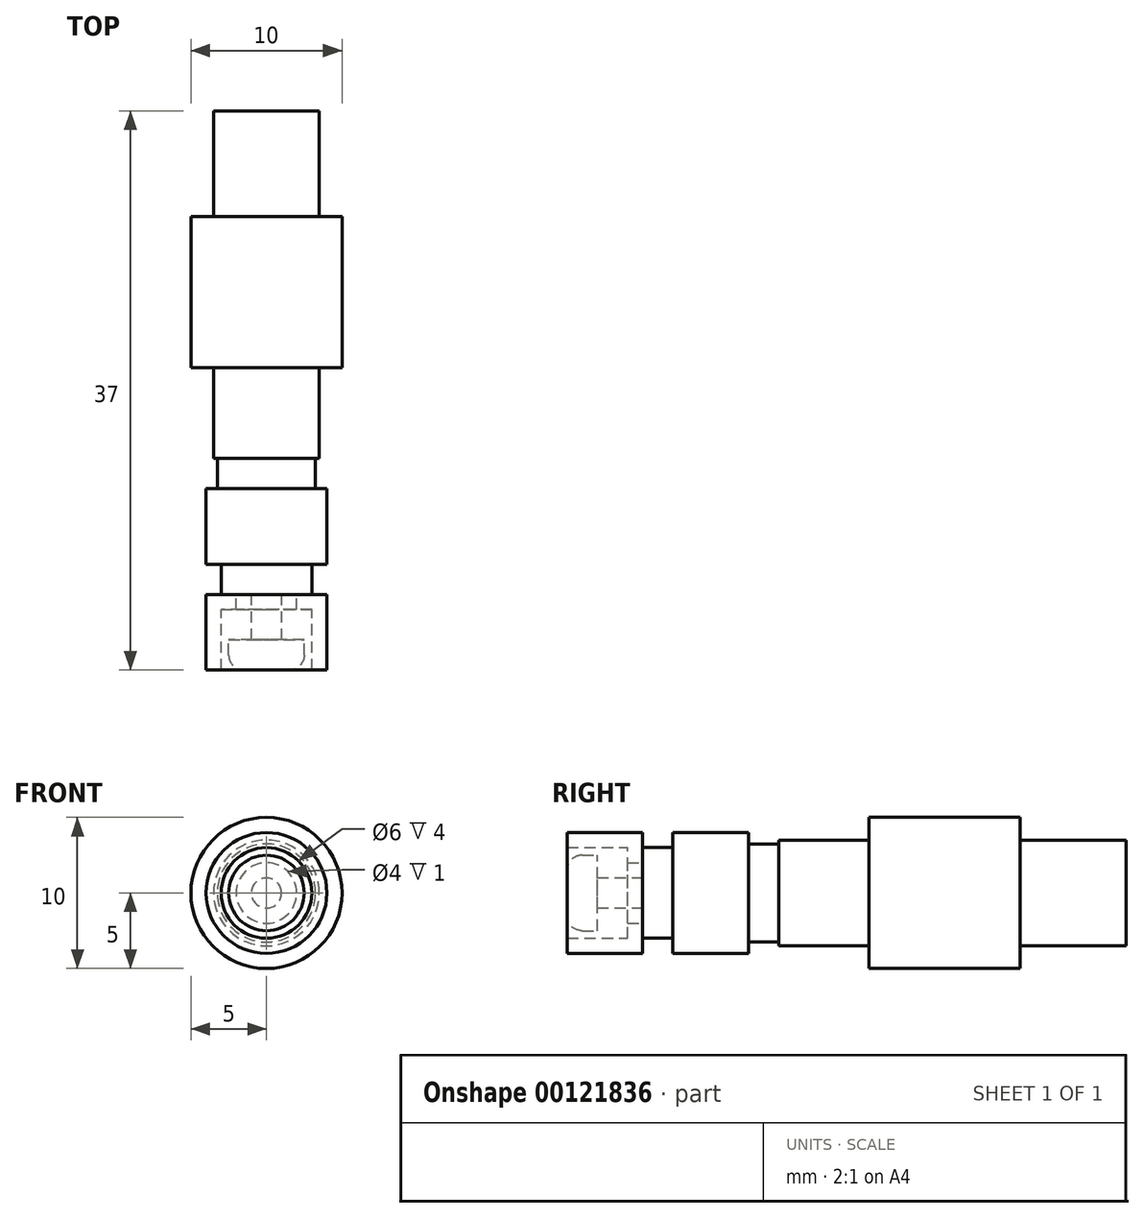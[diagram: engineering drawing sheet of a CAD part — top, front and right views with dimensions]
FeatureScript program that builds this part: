
annotation { "Feature Type Name" : "Feature", "Feature Type Description" : "" }
export const myFeature = defineFeature(function(context is Context, id is Id, definition is map)
    precondition{}
    {
        {
            var Q0;
            Q0=qCreatedBy(makeId("Front.planeOp"),FACE);
            var sketch = newSketch(context, id + "F0", { "sketchPlane" : qUnion([Q0])});
            skCircle(sketch, "E0", {"center": v(0, 0) * mm, "radius": 4 * mm});
            skSolve(sketch);
        }
        {
            var Q0;
            Q0=makeQuery(id+"F0.imprint","IMPRINT",FACE,{"disambiguationData":[TD([[makeQuery(id+"F0.imprint","IMPRINT",EDGE,{"derivedFrom":sQuery(id+"F0.wireOp",EDGE,"E0")}),1.0]])]});
            extrude(context, id + "F1", {"entities" : qUnion([Q0]), "depth" : 5 * mm});
        }
        {
            var Q0;
            Q0=makeQuery(id+"F1.opExtrude","CAP_FACE",FACE,{"disambiguationData":[OSD([sQuery(id+"F0.wireOp",EDGE,"E0")])],"isStart":false});
            var sketch = newSketch(context, id + "F2", { "sketchPlane" : qUnion([Q0])});
            skCircle(sketch, "E1", {"center": v(0, 0) * mm, "radius": 3 * mm});
            skSolve(sketch);
        }
        {
            var Q0;
            Q0=makeQuery(id+"F2.imprint","IMPRINT",FACE,{"disambiguationData":[TD([[makeQuery(id+"F2.imprint","IMPRINT",EDGE,{"derivedFrom":sQuery(id+"F2.wireOp",EDGE,"E1")}),1.0]])]});
            extrude(context, id + "F3", {"entities" : qUnion([Q0]), "operationType" : NewBodyOperationType.ADD, "depth" : 2 * mm});
        }
        {
            var Q0;
            Q0=makeQuery(id+"F3.opExtrude","CAP_FACE",FACE,{"disambiguationData":[OSD([sQuery(id+"F2.wireOp",EDGE,"E1")])],"isStart":false});
            var sketch = newSketch(context, id + "F4", { "sketchPlane" : qUnion([Q0])});
            skCircle(sketch, "E2", {"center": v(0, 0) * mm, "radius": 4 * mm});
            skCircle(sketch, "E3", {"center": v(0, 0) * mm, "radius": 2 * mm});
            skSolve(sketch);
        }
        {
            var Q0;
            Q0=makeQuery(id+"F4.imprint","IMPRINT",FACE,{"disambiguationData":[TD([[makeQuery(id+"F4.imprint","IMPRINT",EDGE,{"derivedFrom":sQuery(id+"F4.wireOp",EDGE,"E2")}),1.0]])]});
            var Q1;
            Q1=sQuery(id+"F4.wireOp",EDGE,"E2");
            extrude(context, id + "F5", {"entities" : qUnion([Q0]), "surfaceEntities" : qUnion([Q1]), "depth" : 5 * mm});
        }
        {
            var Q0;
            Q0=makeQuery(id+"F3.opExtrude","CAP_FACE",FACE,{"disambiguationData":[OSD([sQuery(id+"F2.wireOp",EDGE,"E1")])],"isStart":false});
            var sketch = newSketch(context, id + "F6", { "sketchPlane" : qUnion([Q0])});
            skCircle(sketch, "E4", {"center": v(0, 0) * mm, "radius": 1 * mm});
            skSolve(sketch);
        }
        {
            var Q0;
            Q0=makeQuery(id+"F6.imprint","IMPRINT",FACE,{"disambiguationData":[TD([[makeQuery(id+"F6.imprint","IMPRINT",EDGE,{"derivedFrom":sQuery(id+"F6.wireOp",EDGE,"E4")}),1.0]])]});
            var Q1;
            Q1=sQuery(id+"F6.wireOp",EDGE,"E4");
            extrude(context, id + "F7", {"entities" : qUnion([Q0]), "operationType" : NewBodyOperationType.ADD, "surfaceEntities" : qUnion([Q1]), "depth" : 3 * mm});
        }
        {
            var Q0;
            Q0=makeQuery(id+"F7.opExtrude","CAP_FACE",FACE,{"disambiguationData":[OSD([sQuery(id+"F6.wireOp",EDGE,"E4")])],"isStart":false});
            var sketch = newSketch(context, id + "F8", { "sketchPlane" : qUnion([Q0])});
            skCircle(sketch, "E5", {"center": v(0, 0) * mm, "radius": 2.5 * mm});
            skSolve(sketch);
        }
        {
            var Q0;
            Q0=makeQuery(id+"F8.imprint","IMPRINT",FACE,{"disambiguationData":[TD([[makeQuery(id+"F8.imprint","IMPRINT",EDGE,{"derivedFrom":sQuery(id+"F8.wireOp",EDGE,"E5")}),1.0]])]});
            var Q1;
            Q1=makeQuery(id+"F8.imprint","IMPRINT",FACE,{"disambiguationData":[TD([[makeQuery(id+"F8.imprint","IMPRINT",EDGE,{"derivedFrom":makeQuery(id+"F7.opExtrude","CAP_EDGE",EDGE,{"disambiguationData":[OSD([sQuery(id+"F6.wireOp",EDGE,"E4")])],"isStart":false})}),1.0]])]});
            extrude(context, id + "F9", {"entities" : qUnion([Q0, Q1]), "operationType" : NewBodyOperationType.ADD, "depth" : 2 * mm});
        }
        {
            var Q0;
            Q0=makeQuery(id+"F9.opExtrude","CAP_EDGE",EDGE,{"disambiguationData":[OSD([sQuery(id+"F8.wireOp",EDGE,"E5")])],"isStart":false});
            fillet(context, id + "F10", {"entities" : qUnion([Q0]), "radius" : 1 * mm, "tangentPropagation" : true, "allowEdgeOverflow" : false});
        }
        {
            var Q0;
            Q0=makeQuery(id+"F4.imprint","IMPRINT",FACE,{"disambiguationData":[TD([[makeQuery(id+"F4.imprint","IMPRINT",EDGE,{"derivedFrom":sQuery(id+"F4.wireOp",EDGE,"E2")}),1.0]])]});
            var Q1;
            Q1=makeQuery(id+"F4.imprint","IMPRINT",FACE,{"disambiguationData":[TD([[makeQuery(id+"F4.imprint","IMPRINT",EDGE,{"derivedFrom":sQuery(id+"F4.wireOp",EDGE,"E3")}),-1.0]])]});
            extrude(context, id + "F11", {"entities" : qUnion([Q0, Q1]), "operationType" : NewBodyOperationType.ADD, "depth" : 1 * mm});
        }
        {
            var Q0;
            Q0=makeQuery(id+"F1.opExtrude","CAP_FACE",FACE,{"disambiguationData":[OSD([sQuery(id+"F0.wireOp",EDGE,"E0")])],"isStart":true});
            var sketch = newSketch(context, id + "F12", { "sketchPlane" : qUnion([Q0])});
            skCircle(sketch, "E6", {"center": v(0, 0) * mm, "radius": 3.25 * mm});
            skSolve(sketch);
        }
        {
            var Q0;
            Q0=makeQuery(id+"F12.imprint","IMPRINT",FACE,{"disambiguationData":[TD([[makeQuery(id+"F12.imprint","IMPRINT",EDGE,{"derivedFrom":sQuery(id+"F12.wireOp",EDGE,"E6")}),1.0]])]});
            extrude(context, id + "F13", {"entities" : qUnion([Q0]), "operationType" : NewBodyOperationType.ADD, "depth" : 2 * mm});
        }
        {
            var Q0;
            Q0=makeQuery(id+"F13.opExtrude","CAP_FACE",FACE,{"disambiguationData":[OSD([sQuery(id+"F12.wireOp",EDGE,"E6")])],"isStart":false});
            var sketch = newSketch(context, id + "F14", { "sketchPlane" : qUnion([Q0])});
            skCircle(sketch, "E7", {"center": v(0, 0) * mm, "radius": 3.5 * mm});
            skSolve(sketch);
        }
        {
            var Q0;
            Q0=makeQuery(id+"F14.imprint","IMPRINT",FACE,{"disambiguationData":[TD([[makeQuery(id+"F14.imprint","IMPRINT",EDGE,{"derivedFrom":sQuery(id+"F14.wireOp",EDGE,"E7")}),1.0]])]});
            var Q1;
            Q1=makeQuery(id+"F14.imprint","IMPRINT",FACE,{"disambiguationData":[TD([[makeQuery(id+"F14.imprint","IMPRINT",EDGE,{"derivedFrom":makeQuery(id+"F13.opExtrude","CAP_EDGE",EDGE,{"disambiguationData":[OSD([sQuery(id+"F12.wireOp",EDGE,"E6")])],"isStart":false})}),1.0]])]});
            var Q2;
            Q2=sQuery(id+"F14.wireOp",EDGE,"E7");
            extrude(context, id + "F15", {"entities" : qUnion([Q0, Q1]), "operationType" : NewBodyOperationType.ADD, "surfaceEntities" : qUnion([Q2]), "depth" : 6 * mm});
        }
        {
            var Q0;
            Q0=makeQuery(id+"F15.opExtrude","CAP_FACE",FACE,{"disambiguationData":[OSD([sQuery(id+"F14.wireOp",EDGE,"E7")])],"isStart":false});
            var sketch = newSketch(context, id + "F16", { "sketchPlane" : qUnion([Q0])});
            skCircle(sketch, "E8", {"center": v(0, 0) * mm, "radius": 5 * mm});
            skSolve(sketch);
        }
        {
            var Q0;
            Q0=makeQuery(id+"F16.imprint","IMPRINT",FACE,{"disambiguationData":[TD([[makeQuery(id+"F16.imprint","IMPRINT",EDGE,{"derivedFrom":sQuery(id+"F16.wireOp",EDGE,"E8")}),1.0]])]});
            var Q1;
            Q1=makeQuery(id+"F16.imprint","IMPRINT",FACE,{"disambiguationData":[TD([[makeQuery(id+"F16.imprint","IMPRINT",EDGE,{"derivedFrom":makeQuery(id+"F15.opExtrude","CAP_EDGE",EDGE,{"disambiguationData":[OSD([sQuery(id+"F14.wireOp",EDGE,"E7")])],"isStart":false})}),1.0]])]});
            extrude(context, id + "F17", {"entities" : qUnion([Q0, Q1]), "operationType" : NewBodyOperationType.ADD, "depth" : 10 * mm});
        }
        {
            var Q0;
            Q0=makeQuery(id+"F17.opExtrude","CAP_FACE",FACE,{"disambiguationData":[OSD([sQuery(id+"F16.wireOp",EDGE,"E8")])],"isStart":false});
            var sketch = newSketch(context, id + "F18", { "sketchPlane" : qUnion([Q0])});
            skCircle(sketch, "E9", {"center": v(0, 0) * mm, "radius": 3.5 * mm});
            skSolve(sketch);
        }
        {
            var Q0;
            Q0=makeQuery(id+"F18.imprint","IMPRINT",FACE,{"disambiguationData":[TD([[makeQuery(id+"F18.imprint","IMPRINT",EDGE,{"derivedFrom":sQuery(id+"F18.wireOp",EDGE,"E9")}),1.0]])]});
            extrude(context, id + "F19", {"entities" : qUnion([Q0]), "operationType" : NewBodyOperationType.ADD, "depth" : 7 * mm});
        }
    });
